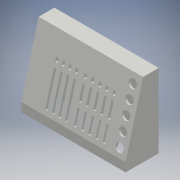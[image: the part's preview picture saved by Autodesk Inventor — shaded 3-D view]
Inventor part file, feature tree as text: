
AUTODESK INVENTOR PART (.ipt)
format: ipt  version: 2018 (Build 220112000, 112)  size: 286,720 bytes
history: native  units: in
note: dims shown in document units (in); Inventor stores cm internally (conversion verified against a paired STEP export)
features: extrude x2, sketch x2, shell x1
ambient origin geometry x8: Origin, YZ Plane, XZ Plane, XY Plane, X Axis, Y Axis, Z Axis, Center Point
bodies: Solid3 (feature_tree)
feature tree (5):
  extrude  "Extrusion5"  Depth=12.4in
  shell  "Shell1"  Thickness=0.2756in
  extrude  "Extrusion8"  Depth=0.3937in
  sketch  "Sketch5"  dims[d61=2.3622in d63=0.3937in d65=3.937in d67=0.3937in d69=1.5748in d71=0.3937in d73=1.9685in d75=0.7874in d90=2.3622in d92=0.3937in d94=3.937in d96=0.3937in d98=1.5748in d100=0.3937in d102=1.9685in d104=0.7874in d178=2.3622in d180=0.3937in d182=3.937in d184=0.3937in d186=1.5748in d188=0.3937in d190=1.9685in d192=0.7874in]
  sketch  "Sketch6"  dims[d214=3.937in d216=0.9449in d218=15.0deg d219=1.8665in d220=12.4in d221=0.0in d226=12.4in d232=4.0059in d233=0.2657in d234=1.7717in d235=0.266in d236=0.5118in d237=0.5118in d238=0.5118in d239=0.2657in d240=0.2657in d241=0.2657in d242=4.0059in d243=4.0059in d244=4.0059in d245=0.0in d246=0.0in d247=0.0in d253=0.5118in d254=0.5118in d255=1.7717in d256=1.7717in d257=1.7717in d258=1.7717in d259=0.5118in d260=0.5118in d261=0.5118in d262=0.2657in d263=0.2657in d264=0.2657in d265=0.2657in d266=0.2657in d267=1.7717in d268=1.7717in d269=1.7717in d270=1.7717in d271=1.7717in d272=0.5906in d273=0.5906in d274=0.5906in d275=0.5906in d276=0.2657in d277=0.2657in d278=0.2657in d279=0.2657in d281=0.5906in d290=0.5906in d291=0.5906in d292=0.5906in d299=0.5118in d307=0.2756in d315=0.9449in d316=0.9449in d317=0.9449in d318=8.0in d319=1.9685in d321=1.4961in d322=0.3937in d324=0.3937in d330=0.0246in d331=1.5748in d333=0.7756in d334=0.3937in d336=0.3937in d339=1.9685in d341=0.3937in d343=1.5748in d345=0.3937in d346=0.315in d347=0.4724in d348=0.0246in d349=1.9685in d351=0.8563in d352=0.3937in d354=0.3937in d356=0.5118in d357=0.5118in d358=0.0in d359=0.3937in d360=0.0in d361=0.0in]
